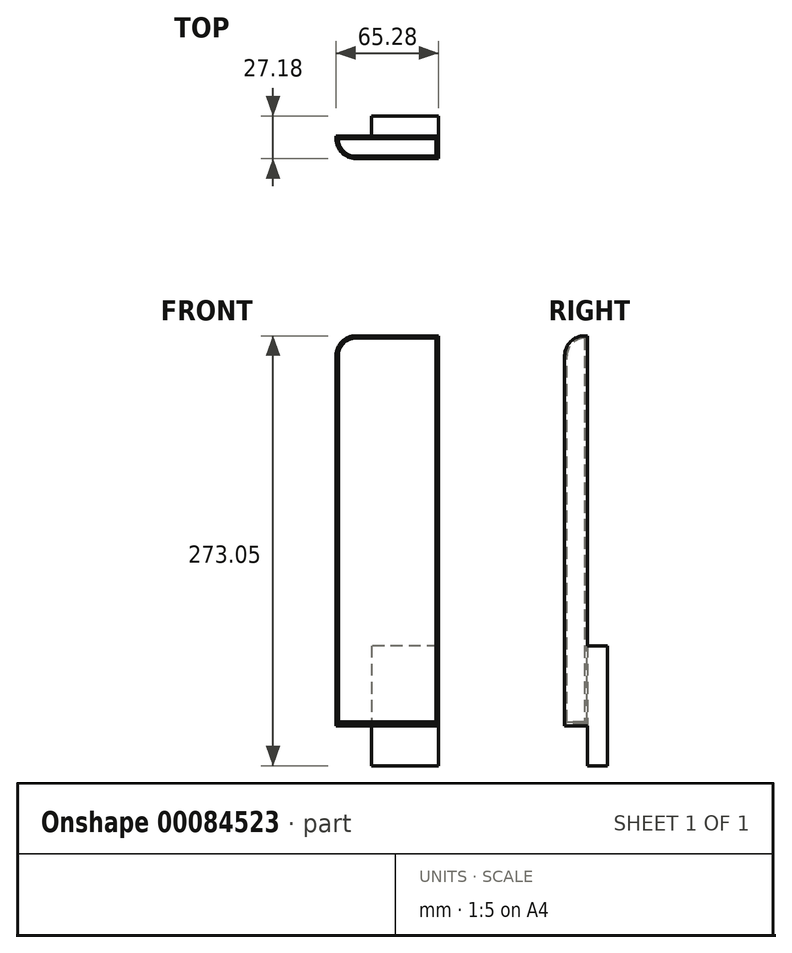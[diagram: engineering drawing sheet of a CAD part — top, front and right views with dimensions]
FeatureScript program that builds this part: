
annotation { "Feature Type Name" : "Feature", "Feature Type Description" : "" }
export const myFeature = defineFeature(function(context is Context, id is Id, definition is map)
    precondition{}
    {
        {
            var Q0;
            Q0=qCreatedBy(makeId("Front.planeOp"),FACE);
            var sketch = newSketch(context, id + "F0", { "sketchPlane" : qUnion([Q0])});
            skLineSegment(sketch, "E0.bottom", {"start": v(63.5, 247.65) * mm, "end": v(0, 247.65) * mm});
            skLineSegment(sketch, "E0.top", {"start": v(63.5, 0) * mm, "end": v(0, 0) * mm});
            skLineSegment(sketch, "E0.left", {"start": v(63.5, 247.65) * mm, "end": v(63.5, 0) * mm});
            skLineSegment(sketch, "E0.right", {"start": v(0, 247.65) * mm, "end": v(0, 0) * mm});
            skSolve(sketch);
        }
        {
            var Q0;
            Q0=qSketchRegion(id+"F0",true);
            extrude(context, id + "F1", {"entities" : qUnion([Q0]), "depth" : 1.78 * mm});
        }
        {
            var Q0;
            Q0=makeQuery(id+"F1.opExtrude","CAP_FACE",FACE,{"disambiguationData":[OSD([sQuery(id+"F0.wireOp",EDGE,"E0.bottom"),sQuery(id+"F0.wireOp",EDGE,"E0.top"),sQuery(id+"F0.wireOp",EDGE,"E0.left"),sQuery(id+"F0.wireOp",EDGE,"E0.right")])],"isStart":false});
            var sketch = newSketch(context, id + "F2", { "sketchPlane" : qUnion([Q0])});
            skLineSegment(sketch, "E1.bottom", {"start": v(0, 0) * mm, "end": v(63.5, 0) * mm});
            skLineSegment(sketch, "E1.top", {"start": v(0, 2.54) * mm, "end": v(63.5, 2.54) * mm});
            skLineSegment(sketch, "E1.left", {"start": v(0, 0) * mm, "end": v(0, 2.54) * mm});
            skLineSegment(sketch, "E1.right", {"start": v(63.5, 0) * mm, "end": v(63.5, 2.54) * mm});
            skSolve(sketch);
        }
        {
            var Q0;
            Q0=qSketchRegion(id+"F2",true);
            extrude(context, id + "F3", {"entities" : qUnion([Q0]), "operationType" : NewBodyOperationType.ADD, "depth" : 12.7 * mm});
        }
        {
            var Q0;
            Q0=makeQuery(id+"F3.boolean.opBoolean","MERGE",FACE,{"derivedFrom":[makeQuery(id+"F1.opExtrude","SWEPT_FACE",FACE,{"disambiguationData":[OSD([sQuery(id+"F0.wireOp",EDGE,"E0.left")])]}),makeQuery(id+"F3.opExtrude","SWEPT_FACE",FACE,{"disambiguationData":[OSD([sQuery(id+"F2.wireOp",EDGE,"E1.right")])]})]});
            var sketch = newSketch(context, id + "F4", { "sketchPlane" : qUnion([Q0])});
            skLineSegment(sketch, "E2.bottom", {"start": v(0, 0) * mm, "end": v(-14.48, 0) * mm});
            skLineSegment(sketch, "E2.top", {"start": v(0, 247.65) * mm, "end": v(-14.48, 247.65) * mm});
            skLineSegment(sketch, "E2.left", {"start": v(0, 0) * mm, "end": v(0, 247.65) * mm});
            skLineSegment(sketch, "E2.right", {"start": v(-14.48, 0) * mm, "end": v(-14.48, 247.65) * mm});
            skSolve(sketch);
        }
        {
            var Q0;
            Q0 = qSketchRegion(id + "F4", true);
            extrude(context, id + "F5", {"entities" : qUnion([Q0]), "operationType" : NewBodyOperationType.ADD, "depth" : 1.78 * mm});
        }
        {
            var Q0;
            Q0=makeQuery(id+"F5.boolean.opBoolean","MERGE",FACE,{"derivedFrom":[makeQuery(id+"F1.opExtrude","CAP_FACE",FACE,{"disambiguationData":[OSD([sQuery(id+"F0.wireOp",EDGE,"E0.bottom"),sQuery(id+"F0.wireOp",EDGE,"E0.top"),sQuery(id+"F0.wireOp",EDGE,"E0.left"),sQuery(id+"F0.wireOp",EDGE,"E0.right")])],"isStart":true}),makeQuery(id+"F5.opExtrude","SWEPT_FACE",FACE,{"disambiguationData":[OSD([sQuery(id+"F4.wireOp",EDGE,"E2.left")])]})]});
            var sketch = newSketch(context, id + "F6", { "sketchPlane" : qUnion([Q0])});
            skLineSegment(sketch, "E3.bottom", {"start": v(-65.28, 50.8) * mm, "end": v(-22.6, 50.8) * mm});
            skLineSegment(sketch, "E3.top", {"start": v(-65.28, -25.4) * mm, "end": v(-22.6, -25.4) * mm});
            skLineSegment(sketch, "E3.left", {"start": v(-65.28, 50.8) * mm, "end": v(-65.28, -25.4) * mm});
            skLineSegment(sketch, "E3.right", {"start": v(-22.6, 50.8) * mm, "end": v(-22.6, -25.4) * mm});
            skSolve(sketch);
        }
        {
            var Q0;
            Q0 = qSketchRegion(id + "F6", true);
            extrude(context, id + "F7", {"entities" : qUnion([Q0]), "operationType" : NewBodyOperationType.ADD, "depth" : 12.7 * mm});
        }
        {
            var Q0;
            Q0=makeQuery(id+"F1.opExtrude","SWEPT_EDGE",EDGE,{"disambiguationData":[OSD([sQuery(id+"F0.wireOp",EDGE,"E0.bottom"),sQuery(id+"F0.wireOp",EDGE,"E0.right")])]});
            var Q1;
            Q1=makeQuery(id+"F5.opExtrude","SWEPT_EDGE",EDGE,{"disambiguationData":[OSD([sQuery(id+"F4.wireOp",EDGE,"E2.top"),sQuery(id+"F4.wireOp",EDGE,"E2.right")])]});
            fillet(context, id + "F8", {"entities" : qUnion([Q0, Q1]), "radius" : 12.7 * mm, "tangentPropagation" : true, "allowEdgeOverflow" : false});
        }
        {
            var Q0;
            Q0=makeQuery(id+"F3.opExtrude","CAP_EDGE",EDGE,{"disambiguationData":[OSD([sQuery(id+"F2.wireOp",EDGE,"E1.left")])],"isStart":false});
            fillet(context, id + "F9", {"entities" : qUnion([Q0]), "radius" : 12.7 * mm, "tangentPropagation" : true, "allowEdgeOverflow" : false});
        }
        {
            var Q0;
            Q0=makeQuery(id+"F1.opExtrude","CAP_EDGE",EDGE,{"disambiguationData":[OSD([sQuery(id+"F0.wireOp",EDGE,"E0.right")])],"isStart":false});
            var Q1;
            Q1=makeQuery(id+"F9.opFillet","BLEND_EDGE",EDGE,{"blendedFrom":[makeQuery(id+"F3.opExtrude","CAP_EDGE",EDGE,{"disambiguationData":[OSD([sQuery(id+"F2.wireOp",EDGE,"E1.left")])],"isStart":false}),makeQuery(id+"F3.opExtrude","SWEPT_FACE",FACE,{"disambiguationData":[OSD([sQuery(id+"F2.wireOp",EDGE,"E1.top")])]})],"blendedInto":[makeQuery(id+"F3.opExtrude","SWEPT_FACE",FACE,{"disambiguationData":[OSD([sQuery(id+"F2.wireOp",EDGE,"E1.top")])]})]});
            var Q2;
            Q2=makeQuery(id+"F5.opExtrude","CAP_EDGE",EDGE,{"disambiguationData":[OSD([sQuery(id+"F4.wireOp",EDGE,"E2.right")])],"isStart":true});
            chamfer(context, id + "F10", {"entities" : qUnion([Q0, Q1, Q2]), "width" : 1.52 * mm, "tangentPropagation" : true});
        }
    });
